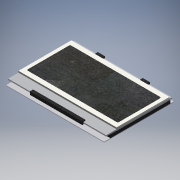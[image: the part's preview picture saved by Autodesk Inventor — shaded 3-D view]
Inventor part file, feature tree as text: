
AUTODESK INVENTOR PART (.ipt)
format: ipt  version: 2017 (Build 210142000, 142)  size: 268,800 bytes
history: native  units: mm
features: extrude x8, sketch x8, projected_geometry x5
ambient origin geometry x8: Origin, YZ Plane, XZ Plane, XY Plane, X Axis, Y Axis, Z Axis, Center Point
bodies: Volumenkörper1 (feature_tree), Volumenkörper3 (feature_tree), Volumenkörper4 (feature_tree), Volumenkörper5 (feature_tree), Volumenkörper6 (feature_tree), Volumenkörper7 (feature_tree), Volumenkörper8 (feature_tree), Volumenkörper9 (feature_tree)
feature tree (21):
  extrude  "LED_Platine"  Depth=67.0mm
  extrude  "LED_Rand"  Depth=3.5mm
  extrude  "LED_Beleuchtung"  Depth=1.3mm
  extrude  "LCD_Back"  Depth=1.3mm
  extrude  "LCD_BackGlas"  Depth=3.0mm TaperAngle=0.0deg
  extrude  "LCD_FrontGlas"  Depth=1.3mm
  extrude  "LCD_AA"  Depth=1.95mm
  extrude  "Extrusion9"  Depth=1.15mm TaperAngle=0.0deg
  sketch  "Skizze1"  dims[d0=94.1mm d1=67.0mm]
  sketch  "Skizze2"  dims[d2=0.55mm d3=0.0mm d4=3.5mm]
  sketch  "Skizze3"  dims[d5=6.0mm d8=1.3mm]
  projected_geometry  "Projizierte Kontur1"
  sketch  "Skizze4"  dims[d9=1.3mm d10=1.3mm]
  sketch  "Skizze5"  dims[d11=7.0mm d12=3.0mm d13=0.0mm]
  projected_geometry  "Projizierte Kontur2"
  sketch  "Skizze6"  dims[d14=3.0mm d15=0.0mm d16=1.3mm]
  projected_geometry  "Projizierte Kontur3"
  sketch  "Skizze7"  dims[d17=0.3mm d18=0.0mm d19=1.95mm]
  projected_geometry  "Projizierte Kontur4"
  sketch  "Skizze8"  dims[d20=1.95mm d21=1.15mm d22=0.0mm d23=2.4mm d24=10.0mm d25=1.5mm d26=0.0mm d27=0.1mm d28=0.0mm d29=3.35mm d30=4.55mm d31=3.35mm d32=4.55mm d33=1.0mm d34=22.0mm d35=7.0mm d36=1.0mm d37=7.0mm d38=2.0mm d39=22.0mm d40=7.0mm d41=1.0mm d42=7.0mm d43=2.0mm d44=22.0mm d45=22.0mm d46=1.0mm d47=2.0mm d48=1.0mm d49=2.0mm d50=0.0mm d51=0.0mm]
  projected_geometry  "Projizierte Kontur5"
